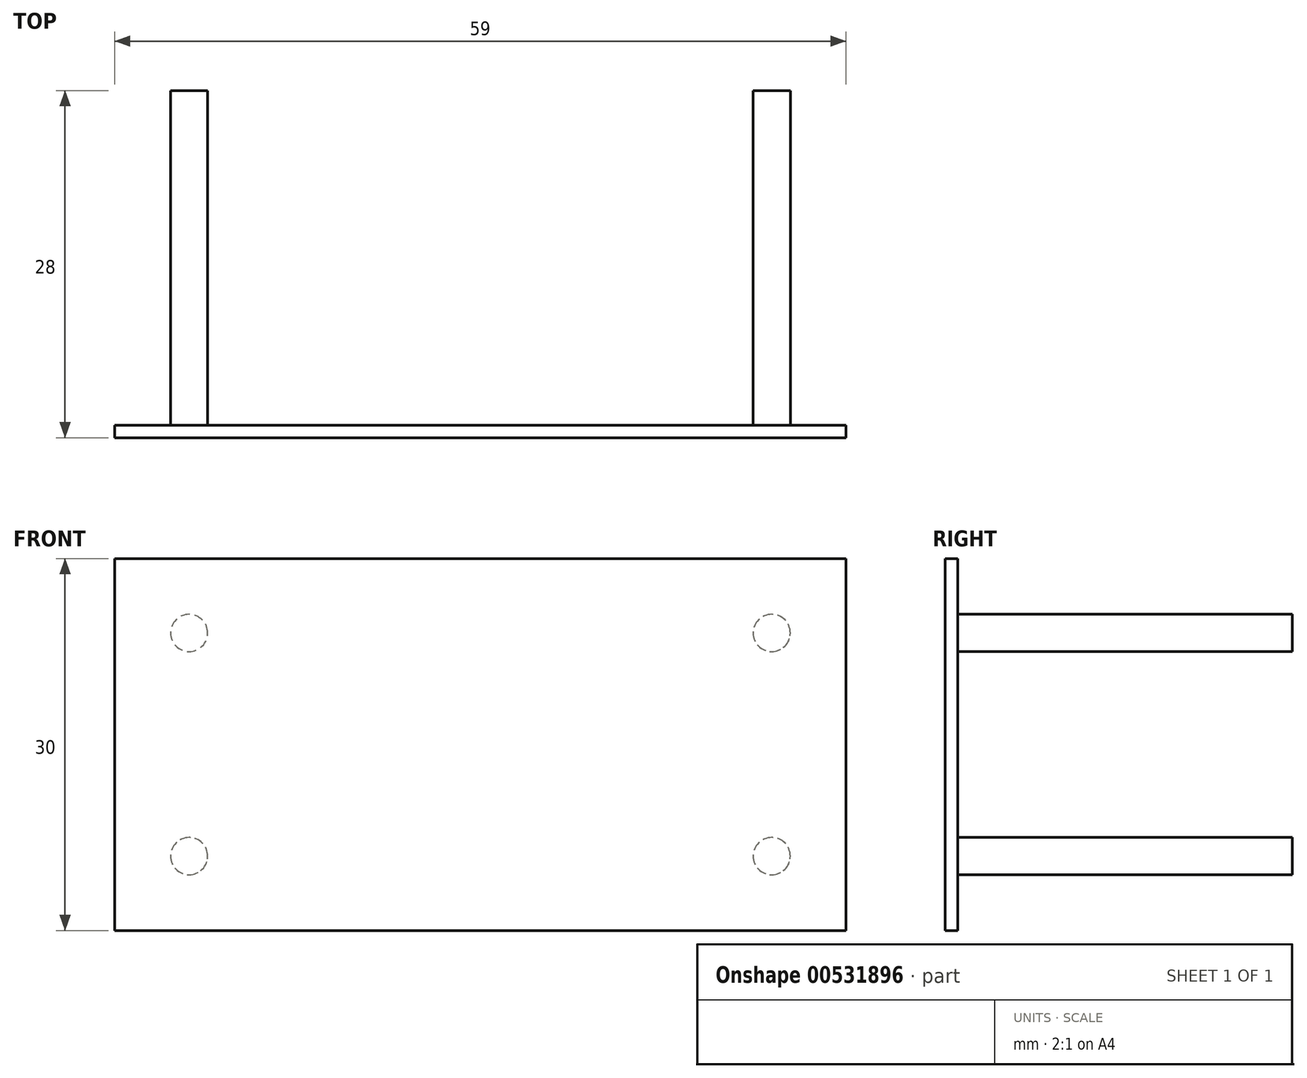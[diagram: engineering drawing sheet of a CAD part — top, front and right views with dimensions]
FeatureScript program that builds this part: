
annotation { "Feature Type Name" : "Feature", "Feature Type Description" : "" }
export const myFeature = defineFeature(function(context is Context, id is Id, definition is map)
    precondition{}
    {
        {
            var Q0;
            Q0=qCreatedBy(makeId("Front.planeOp"),FACE);
            var sketch = newSketch(context, id + "F0", { "sketchPlane" : qUnion([Q0])});
            skLineSegment(sketch, "E0.bottom", {"start": v(29.5, 15) * mm, "end": v(-29.5, 15) * mm});
            skLineSegment(sketch, "E0.top", {"start": v(29.5, -15) * mm, "end": v(-29.5, -15) * mm});
            skLineSegment(sketch, "E0.left", {"start": v(29.5, 15) * mm, "end": v(29.5, -15) * mm});
            skLineSegment(sketch, "E0.right", {"start": v(-29.5, 15) * mm, "end": v(-29.5, -15) * mm});
            skPoint(sketch, "E0.middle", {"position": v(0, 0) * mm});
            skSolve(sketch);
        }
        {
            var Q0;
            Q0 = qSketchRegion(id + "F0", true);
            extrude(context, id + "F1", {"entities" : qUnion([Q0]), "depth" : 1 * mm, "offsetDistance" : 25 * mm});
        }
        {
            var Q0;
            Q0=makeQuery(id+"F1.opExtrude","CAP_FACE",FACE,{"disambiguationData":[OSD([sQuery(id+"F0.wireOp",EDGE,"E0.bottom"),sQuery(id+"F0.wireOp",EDGE,"E0.top"),sQuery(id+"F0.wireOp",EDGE,"E0.left"),sQuery(id+"F0.wireOp",EDGE,"E0.right")])],"isStart":true});
            var sketch = newSketch(context, id + "F2", { "sketchPlane" : qUnion([Q0])});
            skCircle(sketch, "E1", {"center": v(23.5, 9) * mm, "radius": 1.5 * mm});
            skCircle(sketch, "E2", {"center": v(-23.5, 9) * mm, "radius": 1.5 * mm});
            skCircle(sketch, "E3", {"center": v(-23.5, -9) * mm, "radius": 1.5 * mm});
            skCircle(sketch, "E4", {"center": v(23.5, -9) * mm, "radius": 1.5 * mm});
            skSolve(sketch);
        }
        {
            var Q0;
            Q0 = qSketchRegion(id + "F2", true);
            extrude(context, id + "F3", {"entities" : qUnion([Q0]), "operationType" : NewBodyOperationType.ADD, "depth" : 27 * mm, "offsetDistance" : 25 * mm});
        }
    });
